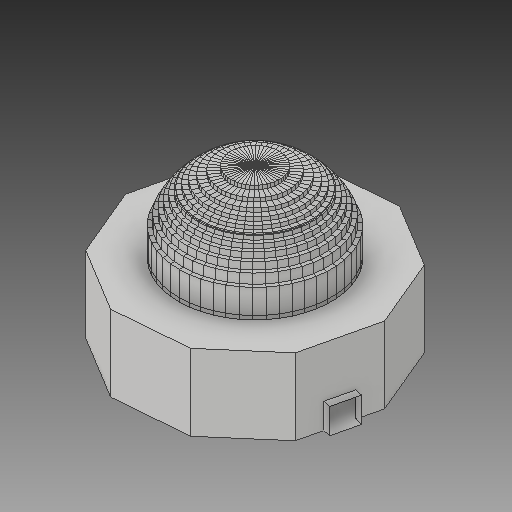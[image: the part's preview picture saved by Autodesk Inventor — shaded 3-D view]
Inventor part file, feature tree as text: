
AUTODESK INVENTOR PART (.ipt)
format: ipt  version: 2017 (Build 210142000, 142)  size: 2,423,296 bytes
history: native  units: in
note: dims shown in document units (in); Inventor stores cm internally (conversion verified against a paired STEP export)
features: extrude x8, sketch x7, other x3, plane x1, pattern_circular x1
ambient origin geometry x8: Origin, YZ Plane, XZ Plane, XY Plane, X Axis, Y Axis, Z Axis, Center Point
bodies: Solid1 (feature_tree)
feature tree (20):
  extrude  "bace"  Depth=1.0in TaperAngle=0.0deg
  extrude  "bace wall"  Depth=20.0in TaperAngle=0.0deg
  extrude  "bace ceiling"  Depth=1.0in
  other  "used to find the workplane for the dome"
  plane  "workplane for dome"
  extrude  "dome make"  Depth=1.0in TaperAngle=0.0deg
  sketch  "Sketch18"  dims[d190=45.0deg d192=1.0in d193=1.0in d194=1.0in d195=1.0in d196=1.0in d197=1.0in d198=1.0in d199=1.0in d200=0.0in d201=1.0in d202=0.0in d204=1.0in d205=19.685in d206=360.0deg d208=1.0in]
  extrude  "dome part cut 1"  Depth=2.5166in TaperAngle=90.0deg
  extrude  "dome part cut 2"  Depth=21.0in
  pattern_circular  "Circular Pattern6"  [2 undecoded]
  extrude  "door frame"  Depth=1.0in
  extrude  "corridor connection"  Depth=1.0in
  other  "Delete Faces of the room"
  other  "Delete Faces of dome"
  sketch  "Sketch1"  dims[d0=62.0in d1=1.0in d2=0.0in]
  sketch  "Sketch2"  dims[d4=1.0in d5=20.0in d6=0.0in]
  sketch  "Sketch3"  dims[d8=1.0in d9=0.0in d16=3.5in d17=6.6667in]
  sketch  "Sketch8"  dims[d18=1.0in d19=0.0in d107=1.0in d108=0.0in]
  sketch  "Sketch12"  dims[d109=40.0in d110=90.0deg d166=2.5166in]
  sketch  "Sketch17"  dims[d186=21.0in d187=0.0in d189=42.0in]
note: 2 required parameter values undecoded (feature->parameter linkage not recoverable at this tier; creation-order binding heuristic only, values carry confidence <= 0.55)
